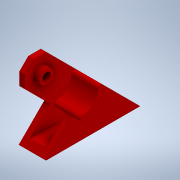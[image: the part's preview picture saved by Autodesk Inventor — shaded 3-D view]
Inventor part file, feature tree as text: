
AUTODESK INVENTOR PART (.ipt)
format: ipt  version: 2020 (Build 240168000, 168)  size: 221,696 bytes
history: native  units: mm
features: extrude x6, sketch x4, projected_geometry x3, plane x1, mirror x1
ambient origin geometry x8: Origin, YZ Plane, XZ Plane, XY Plane, X Axis, Y Axis, Z Axis, Center Point
bodies: Solid1 (feature_tree)
feature tree (15):
  extrude  "Extrusion1"  Depth=30.0mm
  extrude  "Extrusion2"  Depth=13.9mm
  extrude  "Extrusion3"  Depth=15.0mm
  plane  "Work Plane1"
  mirror  "Mirror1"
  extrude  "Extrusion4"  Depth=5.0mm
  sketch  "Sketch5"  dims[d9=0.0mm d10=52.45mm d12=14.45mm d14=7.3mm d15=13.0mm d16=6.0mm d17=0.0mm d18=7.5mm d19=27.8mm d20=0.0mm d21=0.0mm d22=13.9mm d23=5.0mm d24=5.0mm d25=0.0mm d26=19.5mm d27=0.0mm d28=5.0mm]
  extrude  "Extrusion5"  Depth=5.0mm
  extrude  "Extrusion6"  Depth=5.0mm
  sketch  "Sketch2"  dims[d0=45.0deg d1=30.0mm]
  projected_geometry  "Projected Loop1"
  sketch  "Sketch3"  dims[d2=5.0mm d4=13.9mm]
  projected_geometry  "Projected Loop2"
  sketch  "Sketch4"  dims[d5=5.0mm d6=0.0mm d8=15.0mm]
  projected_geometry  "Projected Loop3"
